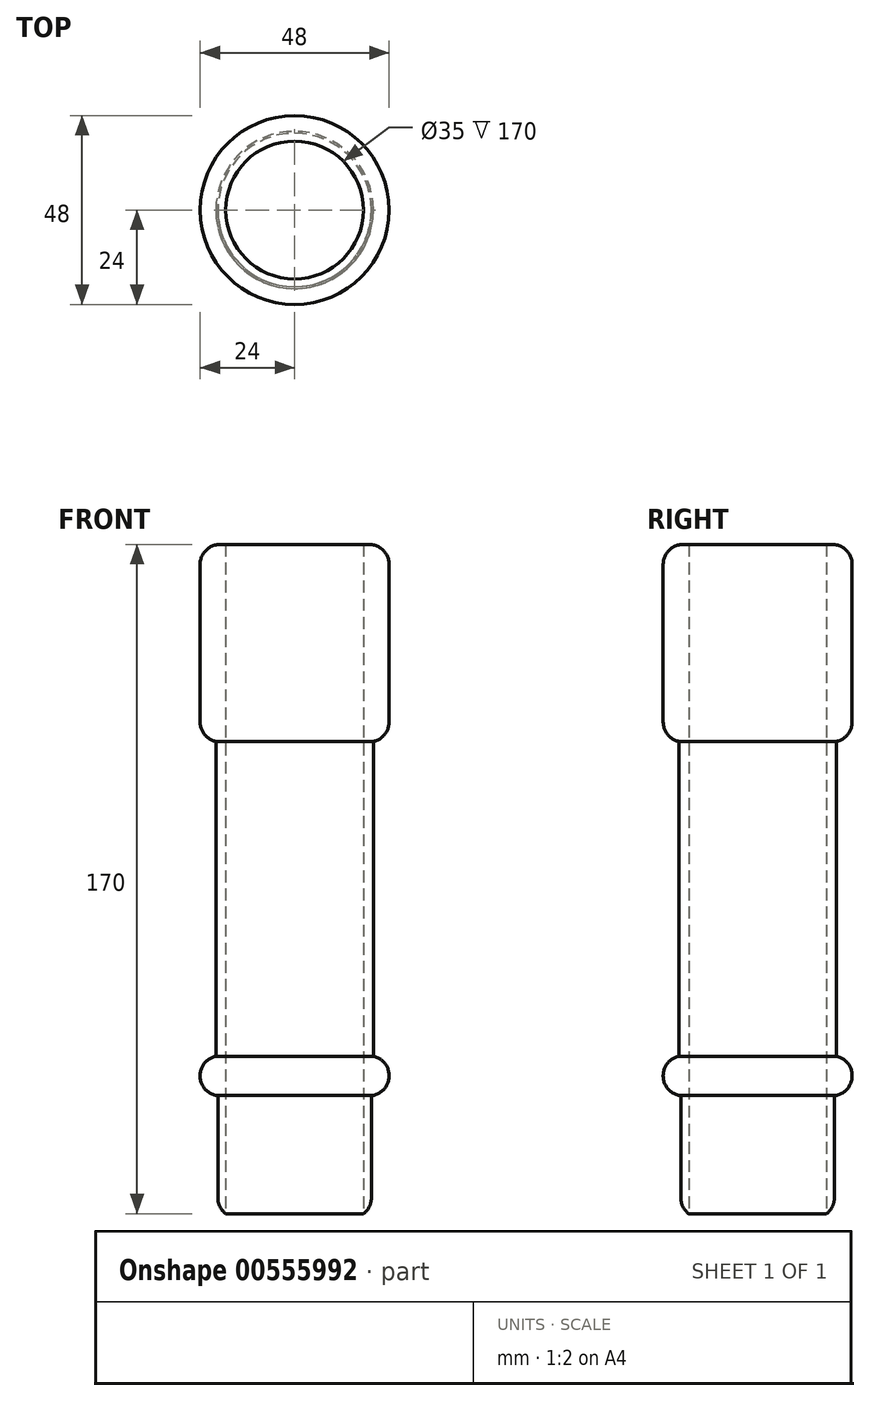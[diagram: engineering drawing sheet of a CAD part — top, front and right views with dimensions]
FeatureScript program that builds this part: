
annotation { "Feature Type Name" : "Feature", "Feature Type Description" : "" }
export const myFeature = defineFeature(function(context is Context, id is Id, definition is map)
    precondition{}
    {
        {
            var Q0;
            Q0=qCreatedBy(makeId("Top.planeOp"),FACE);
            var sketch = newSketch(context, id + "F0", { "sketchPlane" : qUnion([Q0])});
            skCircle(sketch, "E0", {"center": v(0, 0) * mm, "radius": 19.5 * mm});
            skCircle(sketch, "E1", {"center": v(0, 0) * mm, "radius": 17.5 * mm});
            skSolve(sketch);
        }
        {
            var Q0;
            Q0=makeQuery(id+"F0.imprint","IMPRINT",FACE,{"disambiguationData":[TD([[makeQuery(id+"F0.imprint","IMPRINT",EDGE,{"derivedFrom":sQuery(id+"F0.wireOp",EDGE,"E0")}),1.0]])]});
            extrude(context, id + "F1", {"entities" : qUnion([Q0]), "depth" : 30 * mm, "offsetDistance" : 25 * mm});
        }
        {
            var Q0;
            Q0=makeQuery(id+"F1.opExtrude","CAP_FACE",FACE,{"disambiguationData":[OSD([sQuery(id+"F0.wireOp",EDGE,"E0"),sQuery(id+"F0.wireOp",EDGE,"E1")])],"isStart":false});
            var sketch = newSketch(context, id + "F2", { "sketchPlane" : qUnion([Q0])});
            skCircle(sketch, "E2", {"center": v(0, 0) * mm, "radius": 17.5 * mm});
            skCircle(sketch, "E3", {"center": v(0, 0) * mm, "radius": 24 * mm});
            skSolve(sketch);
        }
        {
            var Q0;
            Q0=makeQuery(id+"F2.imprint","IMPRINT",FACE,{"disambiguationData":[TD([[makeQuery(id+"F2.imprint","IMPRINT",EDGE,{"derivedFrom":sQuery(id+"F2.wireOp",EDGE,"E3")}),1.0]])]});
            var Q1;
            Q1=makeQuery(id+"F2.imprint","IMPRINT",FACE,{"disambiguationData":[TD([[makeQuery(id+"F2.imprint","IMPRINT",EDGE,{"derivedFrom":sQuery(id+"F2.wireOp",EDGE,"E2")}),-1.0]])]});
            extrude(context, id + "F3", {"entities" : qUnion([Q0, Q1]), "operationType" : NewBodyOperationType.ADD, "depth" : 10 * mm, "offsetDistance" : 25 * mm});
        }
        {
            var Q0;
            Q0=makeQuery(id+"F3.opExtrude","CAP_FACE",FACE,{"disambiguationData":[OSD([sQuery(id+"F2.wireOp",EDGE,"E2"),sQuery(id+"F2.wireOp",EDGE,"E3")])],"isStart":false});
            var sketch = newSketch(context, id + "F4", { "sketchPlane" : qUnion([Q0])});
            skCircle(sketch, "E4", {"center": v(0, 0) * mm, "radius": 17.5 * mm});
            skCircle(sketch, "E5", {"center": v(0, 0) * mm, "radius": 20 * mm});
            skSolve(sketch);
        }
        {
            var Q0;
            Q0=makeQuery(id+"F4.imprint","IMPRINT",FACE,{"disambiguationData":[TD([[makeQuery(id+"F4.imprint","IMPRINT",EDGE,{"derivedFrom":sQuery(id+"F4.wireOp",EDGE,"E4")}),-1.0]])]});
            extrude(context, id + "F5", {"entities" : qUnion([Q0]), "operationType" : NewBodyOperationType.ADD, "depth" : 80 * mm, "offsetDistance" : 25 * mm});
        }
        {
            var Q0;
            Q0=makeQuery(id+"F5.opExtrude","CAP_FACE",FACE,{"disambiguationData":[OSD([sQuery(id+"F4.wireOp",EDGE,"E4"),sQuery(id+"F4.wireOp",EDGE,"E5")])],"isStart":false});
            var sketch = newSketch(context, id + "F6", { "sketchPlane" : qUnion([Q0])});
            skCircle(sketch, "E6", {"center": v(0, 0) * mm, "radius": 17.5 * mm});
            skCircle(sketch, "E7", {"center": v(0, 0) * mm, "radius": 24 * mm});
            skSolve(sketch);
        }
        {
            var Q0;
            Q0 = qSketchRegion(id + "F6", true);
            extrude(context, id + "F7", {"entities" : qUnion([Q0]), "operationType" : NewBodyOperationType.ADD, "depth" : 50 * mm, "offsetDistance" : 25 * mm});
        }
        {
            var Q0;
            Q0=makeQuery(id+"F7.opExtrude","CAP_EDGE",EDGE,{"disambiguationData":[OSD([sQuery(id+"F6.wireOp",EDGE,"E7")])],"isStart":false});
            var Q1;
            Q1=makeQuery(id+"F7.opExtrude","CAP_EDGE",EDGE,{"disambiguationData":[OSD([sQuery(id+"F6.wireOp",EDGE,"E7")])],"isStart":true});
            var Q2;
            Q2=makeQuery(id+"F3.opExtrude","CAP_EDGE",EDGE,{"disambiguationData":[OSD([sQuery(id+"F2.wireOp",EDGE,"E3")])],"isStart":false});
            var Q3;
            Q3=makeQuery(id+"F3.opExtrude","CAP_EDGE",EDGE,{"disambiguationData":[OSD([sQuery(id+"F2.wireOp",EDGE,"E3")])],"isStart":true});
            var Q4;
            Q4=makeQuery(id+"F1.opExtrude","CAP_EDGE",EDGE,{"disambiguationData":[OSD([sQuery(id+"F0.wireOp",EDGE,"E0")])],"isStart":true});
            fillet(context, id + "F8", {"entities" : qUnion([Q0, Q1, Q2, Q3, Q4]), "radius" : 5 * mm, "tangentPropagation" : true, "allowEdgeOverflow" : false});
        }
    });
